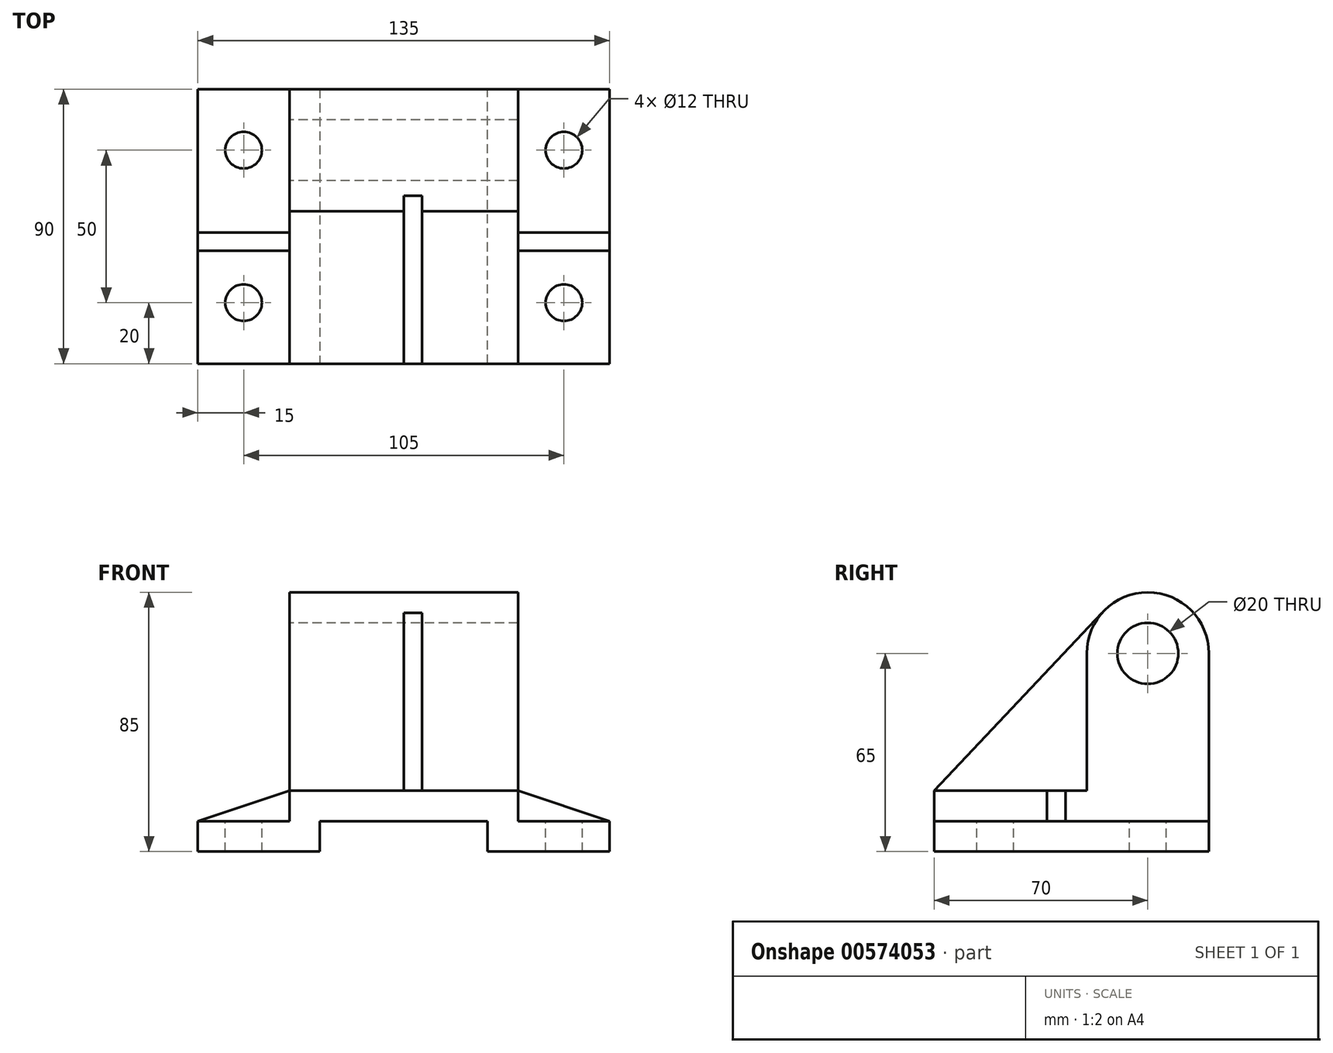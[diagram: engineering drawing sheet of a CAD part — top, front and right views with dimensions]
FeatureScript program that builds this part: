
annotation { "Feature Type Name" : "Feature", "Feature Type Description" : "" }
export const myFeature = defineFeature(function(context is Context, id is Id, definition is map)
    precondition{}
    {
        {
            var Q0;
            Q0=qCreatedBy(makeId("Top.planeOp"),FACE);
            var sketch = newSketch(context, id + "F0", { "sketchPlane" : qUnion([Q0])});
            skLineSegment(sketch, "E0.bottom", {"start": v(67.5, -45) * mm, "end": v(-67.5, -45) * mm});
            skLineSegment(sketch, "E0.top", {"start": v(67.5, 45) * mm, "end": v(-67.5, 45) * mm});
            skLineSegment(sketch, "E0.left", {"start": v(67.5, -45) * mm, "end": v(67.5, 45) * mm});
            skLineSegment(sketch, "E0.right", {"start": v(-67.5, -45) * mm, "end": v(-67.5, 45) * mm});
            skPoint(sketch, "E0.middle", {"position": v(0, 0) * mm});
            skSolve(sketch);
        }
        {
            var Q0;
            Q0 = qSketchRegion(id + "F0", true);
            extrude(context, id + "F1", {"entities" : qUnion([Q0]), "depth" : 20 * mm, "offsetDistance" : 25 * mm});
        }
        {
            var Q0;
            Q0=makeQuery(id+"F1.opExtrude","SWEPT_FACE",FACE,{"disambiguationData":[OSD([sQuery(id+"F0.wireOp",EDGE,"E0.bottom")])]});
            var sketch = newSketch(context, id + "F2", { "sketchPlane" : qUnion([Q0])});
            skLineSegment(sketch, "E1", {"start": v(0, 0) * mm, "end": v(0, 10) * mm, "construction": true});
            skLineSegment(sketch, "E2", {"start": v(-27.5, 10) * mm, "end": v(-27.5, -4.94) * mm});
            skLineSegment(sketch, "E3", {"start": v(-27.5, -4.94) * mm, "end": v(27.5, -4.94) * mm});
            skLineSegment(sketch, "E4", {"start": v(27.5, -4.94) * mm, "end": v(27.5, 10) * mm});
            skLineSegment(sketch, "E5", {"start": v(-27.5, 10) * mm, "end": v(27.5, 10) * mm});
            skSolve(sketch);
        }
        {
            var Q0;
            Q0 = qSketchRegion(id + "F2", true);
            var Q1;
            Q1=makeQuery(id+"F1.opExtrude","SWEPT_FACE",FACE,{"disambiguationData":[OSD([sQuery(id+"F0.wireOp",EDGE,"E0.top")])]});
            extrude(context, id + "F3", {"entities" : qUnion([Q0]), "operationType" : NewBodyOperationType.REMOVE, "endBound" : BoundingType.UP_TO_SURFACE, "oppositeDirection" : true, "depth" : 25 * mm, "endBoundEntityFace" : qUnion([Q1]), "offsetDistance" : 25 * mm});
        }
        {
            var Q0;
            Q0=makeQuery(id+"F1.opExtrude","SWEPT_FACE",FACE,{"disambiguationData":[OSD([sQuery(id+"F0.wireOp",EDGE,"E0.bottom")])]});
            var sketch = newSketch(context, id + "F4", { "sketchPlane" : qUnion([Q0])});
            skLineSegment(sketch, "E6", {"start": v(-67.5, 10) * mm, "end": v(-37.5, 10) * mm, "construction": true});
            skLineSegment(sketch, "E7", {"start": v(-37.5, 10) * mm, "end": v(-37.5, 27.32) * mm});
            skLineSegment(sketch, "E8", {"start": v(-37.5, 27.32) * mm, "end": v(-72.8, 27.32) * mm});
            skLineSegment(sketch, "E9", {"start": v(-72.8, 27.32) * mm, "end": v(-72.8, 10) * mm});
            skLineSegment(sketch, "E10", {"start": v(-72.8, 10) * mm, "end": v(-37.5, 10) * mm});
            skLineSegment(sketch, "E11", {"start": v(0, 0) * mm, "end": v(0, 28.68) * mm, "construction": true});
            skPoint(sketch, "E11.endSnap0", {"position": v(0, 10) * mm});
            skLineSegment(sketch, "E12.MirrorCS", {"start": v(37.5, 27.32) * mm, "end": v(72.8, 27.32) * mm});
            skLineSegment(sketch, "E13.MirrorCS", {"start": v(72.8, 27.32) * mm, "end": v(72.8, 10) * mm});
            skLineSegment(sketch, "E14.MirrorCS", {"start": v(37.5, 10) * mm, "end": v(37.5, 27.32) * mm});
            skLineSegment(sketch, "E15.MirrorCS", {"start": v(72.8, 10) * mm, "end": v(37.5, 10) * mm});
            skSolve(sketch);
        }
        {
            var Q0;
            Q0 = qSketchRegion(id + "F4", true);
            extrude(context, id + "F5", {"entities" : qUnion([Q0]), "operationType" : NewBodyOperationType.REMOVE, "oppositeDirection" : true, "depth" : 37 * mm, "offsetDistance" : 25 * mm});
        }
        {
            var Q0;
            Q0=makeQuery(id+"F1.opExtrude","SWEPT_FACE",FACE,{"disambiguationData":[OSD([sQuery(id+"F0.wireOp",EDGE,"E0.top")])]});
            var sketch = newSketch(context, id + "F6", { "sketchPlane" : qUnion([Q0])});
            skLineSegment(sketch, "E16", {"start": v(-67.5, 10) * mm, "end": v(-37.5, 10) * mm, "construction": true});
            skLineSegment(sketch, "E17", {"start": v(-37.5, 10) * mm, "end": v(-37.5, 24.06) * mm});
            skLineSegment(sketch, "E18", {"start": v(-37.5, 24.06) * mm, "end": v(-71.47, 24.06) * mm});
            skLineSegment(sketch, "E19", {"start": v(-71.47, 24.06) * mm, "end": v(-71.47, 10) * mm});
            skLineSegment(sketch, "E20", {"start": v(-71.47, 10) * mm, "end": v(-37.5, 10) * mm});
            skLineSegment(sketch, "E21", {"start": v(0, 6.86) * mm, "end": v(0, 24.8) * mm, "construction": true});
            skPoint(sketch, "E21.endSnap0", {"position": v(0, 10) * mm});
            skLineSegment(sketch, "E22.MirrorCS", {"start": v(37.5, 24.06) * mm, "end": v(71.47, 24.06) * mm});
            skLineSegment(sketch, "E23.MirrorCS", {"start": v(71.47, 24.06) * mm, "end": v(71.47, 10) * mm});
            skLineSegment(sketch, "E24.MirrorCS", {"start": v(37.5, 10) * mm, "end": v(37.5, 24.06) * mm});
            skLineSegment(sketch, "E25.MirrorCS", {"start": v(71.47, 10) * mm, "end": v(37.5, 10) * mm});
            skSolve(sketch);
        }
        {
            var Q0;
            Q0 = qSketchRegion(id + "F6", true);
            extrude(context, id + "F7", {"entities" : qUnion([Q0]), "operationType" : NewBodyOperationType.REMOVE, "oppositeDirection" : true, "depth" : 47 * mm, "offsetDistance" : 25 * mm});
        }
        {
            var Q0;
            Q0=makeQuery(id+"F5.boolean.opBoolean","COPY",FACE,{"derivedFrom":makeQuery(id+"F5.opExtrude","CAP_FACE",FACE,{"disambiguationData":[OSD([sQuery(id+"F4.wireOp",EDGE,"E7"),sQuery(id+"F4.wireOp",EDGE,"E8"),sQuery(id+"F4.wireOp",EDGE,"E9"),sQuery(id+"F4.wireOp",EDGE,"E10")])],"isStart":false})});
            var sketch = newSketch(context, id + "F8", { "sketchPlane" : qUnion([Q0])});
            skLineSegment(sketch, "E26", {"start": v(-67.5, 10) * mm, "end": v(-37.5, 20) * mm});
            skLineSegment(sketch, "E27", {"start": v(-37.5, 20) * mm, "end": v(-37.5, 24.23) * mm});
            skLineSegment(sketch, "E28", {"start": v(-37.5, 24.23) * mm, "end": v(-69.8, 24.23) * mm});
            skLineSegment(sketch, "E29", {"start": v(-69.8, 24.23) * mm, "end": v(-69.8, 10) * mm});
            skLineSegment(sketch, "E30", {"start": v(-69.8, 10) * mm, "end": v(-67.5, 10) * mm});
            skLineSegment(sketch, "E31", {"start": v(0, 0) * mm, "end": v(0, 26.12) * mm, "construction": true});
            skLineSegment(sketch, "E32.MirrorCS", {"start": v(37.5, 24.23) * mm, "end": v(69.8, 24.23) * mm});
            skLineSegment(sketch, "E33.MirrorCS", {"start": v(37.5, 20) * mm, "end": v(37.5, 24.23) * mm});
            skLineSegment(sketch, "E34.MirrorCS", {"start": v(67.5, 10) * mm, "end": v(37.5, 20) * mm});
            skLineSegment(sketch, "E35.MirrorCS", {"start": v(69.8, 24.23) * mm, "end": v(69.8, 10) * mm});
            skLineSegment(sketch, "E36.MirrorCS", {"start": v(69.8, 10) * mm, "end": v(67.5, 10) * mm});
            skSolve(sketch);
        }
        {
            var Q0;
            Q0 = qSketchRegion(id + "F8", true);
            var Q1;
            Q1=makeQuery(id+"F7.boolean.opBoolean","COPY",FACE,{"derivedFrom":makeQuery(id+"F7.opExtrude","CAP_FACE",FACE,{"disambiguationData":[OSD([sQuery(id+"F6.wireOp",EDGE,"E17"),sQuery(id+"F6.wireOp",EDGE,"E18"),sQuery(id+"F6.wireOp",EDGE,"E19"),sQuery(id+"F6.wireOp",EDGE,"E20")])],"isStart":false})});
            extrude(context, id + "F9", {"entities" : qUnion([Q0]), "operationType" : NewBodyOperationType.REMOVE, "endBound" : BoundingType.UP_TO_SURFACE, "oppositeDirection" : true, "depth" : 25 * mm, "endBoundEntityFace" : qUnion([Q1]), "offsetDistance" : 25 * mm});
        }
        {
            var Q0;
            Q0=makeQuery(id+"F7.boolean.opBoolean","COPY",FACE,{"derivedFrom":makeQuery(id+"F7.opExtrude","SWEPT_FACE",FACE,{"disambiguationData":[OSD([sQuery(id+"F6.wireOp",EDGE,"E24.MirrorCS")])]})});
            var sketch = newSketch(context, id + "F10", { "sketchPlane" : qUnion([Q0])});
            skLineSegment(sketch, "E37", {"start": v(-45, 20) * mm, "end": v(-45, 65) * mm});
            skLineSegment(sketch, "E38", {"start": v(-45, 20) * mm, "end": v(-5, 20) * mm});
            skLineSegment(sketch, "E39", {"start": v(-5, 20) * mm, "end": v(-5, 65) * mm});
            skArc(sketch, "E40", {"start": v(-5, 65) * mm, "mid": v(-25, 85) * mm, "end": v(-45, 65) * mm});
            skSolve(sketch);
        }
        {
            var Q0;
            Q0 = qSketchRegion(id + "F10", true);
            var Q1;
            Q1=makeQuery(id+"F7.boolean.opBoolean","COPY",FACE,{"derivedFrom":makeQuery(id+"F7.opExtrude","SWEPT_FACE",FACE,{"disambiguationData":[OSD([sQuery(id+"F6.wireOp",EDGE,"E17")])]})});
            extrude(context, id + "F11", {"entities" : qUnion([Q0]), "operationType" : NewBodyOperationType.ADD, "endBound" : BoundingType.UP_TO_SURFACE, "oppositeDirection" : true, "depth" : 25 * mm, "endBoundEntityFace" : qUnion([Q1]), "offsetDistance" : 25 * mm});
        }
        {
            var Q0;
            Q0=makeQuery(id+"F11.boolean.opBoolean","MERGE",FACE,{"derivedFrom":[makeQuery(id+"F7.boolean.opBoolean","COPY",FACE,{"derivedFrom":makeQuery(id+"F7.opExtrude","SWEPT_FACE",FACE,{"disambiguationData":[OSD([sQuery(id+"F6.wireOp",EDGE,"E24.MirrorCS")])]})}),makeQuery(id+"F11.opExtrude","CAP_FACE",FACE,{"disambiguationData":[OSD([sQuery(id+"F10.wireOp",EDGE,"E37"),sQuery(id+"F10.wireOp",EDGE,"E38"),sQuery(id+"F10.wireOp",EDGE,"E39"),sQuery(id+"F10.wireOp",EDGE,"E40")])],"isStart":true})]});
            var sketch = newSketch(context, id + "F12", { "sketchPlane" : qUnion([Q0])});
            skCircle(sketch, "E41", {"center": v(-25, 65) * mm, "radius": 10 * mm});
            skSolve(sketch);
        }
        {
            var Q0;
            Q0 = qSketchRegion(id + "F12", true);
            extrude(context, id + "F13", {"entities" : qUnion([Q0]), "operationType" : NewBodyOperationType.REMOVE, "endBound" : BoundingType.THROUGH_ALL, "oppositeDirection" : true, "depth" : 25 * mm, "offsetDistance" : 25 * mm});
        }
        {
            var Q0;
            Q0=makeQuery(id+"F5.boolean.opBoolean","COPY",FACE,{"derivedFrom":makeQuery(id+"F5.opExtrude","SWEPT_FACE",FACE,{"disambiguationData":[OSD([sQuery(id+"F4.wireOp",EDGE,"E10")])]})});
            var sketch = newSketch(context, id + "F14", { "sketchPlane" : qUnion([Q0])});
            skLineSegment(sketch, "E42", {"start": v(-67.5, -45) * mm, "end": v(-52.5, -45) * mm, "construction": true});
            skLineSegment(sketch, "E43", {"start": v(-52.5, -45) * mm, "end": v(-52.5, -25) * mm, "construction": true});
            skCircle(sketch, "E44", {"center": v(-52.5, -25) * mm, "radius": 6 * mm});
            skLineSegment(sketch, "E45", {"start": v(-52.5, -25) * mm, "end": v(-52.5, 0) * mm, "construction": true});
            skLineSegment(sketch, "E46", {"start": v(-52.5, 0) * mm, "end": v(-74.7, 0) * mm, "construction": true});
            skCircle(sketch, "E47.MirrorC", {"center": v(-52.5, 25) * mm, "radius": 6 * mm});
            skLineSegment(sketch, "E48", {"start": v(0, -45) * mm, "end": v(0, 45.24) * mm, "construction": true});
            skCircle(sketch, "E49.MirrorC", {"center": v(52.5, -25) * mm, "radius": 6 * mm});
            skCircle(sketch, "E50.MirrorC", {"center": v(52.5, 25) * mm, "radius": 6 * mm});
            skSolve(sketch);
        }
        {
            var Q0;
            Q0 = qSketchRegion(id + "F14", true);
            extrude(context, id + "F15", {"entities" : qUnion([Q0]), "operationType" : NewBodyOperationType.REMOVE, "endBound" : BoundingType.THROUGH_ALL, "oppositeDirection" : true, "depth" : 25 * mm, "offsetDistance" : 25 * mm});
        }
        {
            var Q0;
            Q0=makeQuery(id+"F1.opExtrude","CAP_FACE",FACE,{"disambiguationData":[OSD([sQuery(id+"F0.wireOp",EDGE,"E0.bottom"),sQuery(id+"F0.wireOp",EDGE,"E0.top"),sQuery(id+"F0.wireOp",EDGE,"E0.left"),sQuery(id+"F0.wireOp",EDGE,"E0.right")])],"isStart":false});
            var sketch = newSketch(context, id + "F16", { "sketchPlane" : qUnion([Q0])});
            skLineSegment(sketch, "E51", {"start": v(6, -45) * mm, "end": v(0, -45) * mm});
            skLineSegment(sketch, "E52", {"start": v(0, -45) * mm, "end": v(0, 10) * mm});
            skLineSegment(sketch, "E53", {"start": v(0, 10) * mm, "end": v(6, 10) * mm});
            skLineSegment(sketch, "E54", {"start": v(6, 10) * mm, "end": v(6, -45) * mm});
            skSolve(sketch);
        }
        {
            var Q0;
            Q0 = qSketchRegion(id + "F16", true);
            extrude(context, id + "F17", {"entities" : qUnion([Q0]), "operationType" : NewBodyOperationType.ADD, "depth" : 65 * mm, "offsetDistance" : 25 * mm});
        }
        {
            var Q0;
            Q0=makeQuery(id+"F17.opExtrude","SWEPT_FACE",FACE,{"disambiguationData":[OSD([sQuery(id+"F16.wireOp",EDGE,"E52")])]});
            var sketch = newSketch(context, id + "F18", { "sketchPlane" : qUnion([Q0])});
            skLineSegment(sketch, "E55", {"start": v(45, 20) * mm, "end": v(-10, 78.23) * mm});
            skLineSegment(sketch, "E56", {"start": v(-10, 78.23) * mm, "end": v(-10, 85) * mm});
            skLineSegment(sketch, "E57", {"start": v(-10, 85) * mm, "end": v(45, 85) * mm});
            skLineSegment(sketch, "E58", {"start": v(45, 85) * mm, "end": v(45, 20) * mm});
            skSolve(sketch);
        }
        {
            var Q0;
            Q0 = qSketchRegion(id + "F18", true);
            extrude(context, id + "F19", {"entities" : qUnion([Q0]), "operationType" : NewBodyOperationType.REMOVE, "oppositeDirection" : true, "depth" : 6 * mm, "offsetDistance" : 25 * mm});
        }
    });
